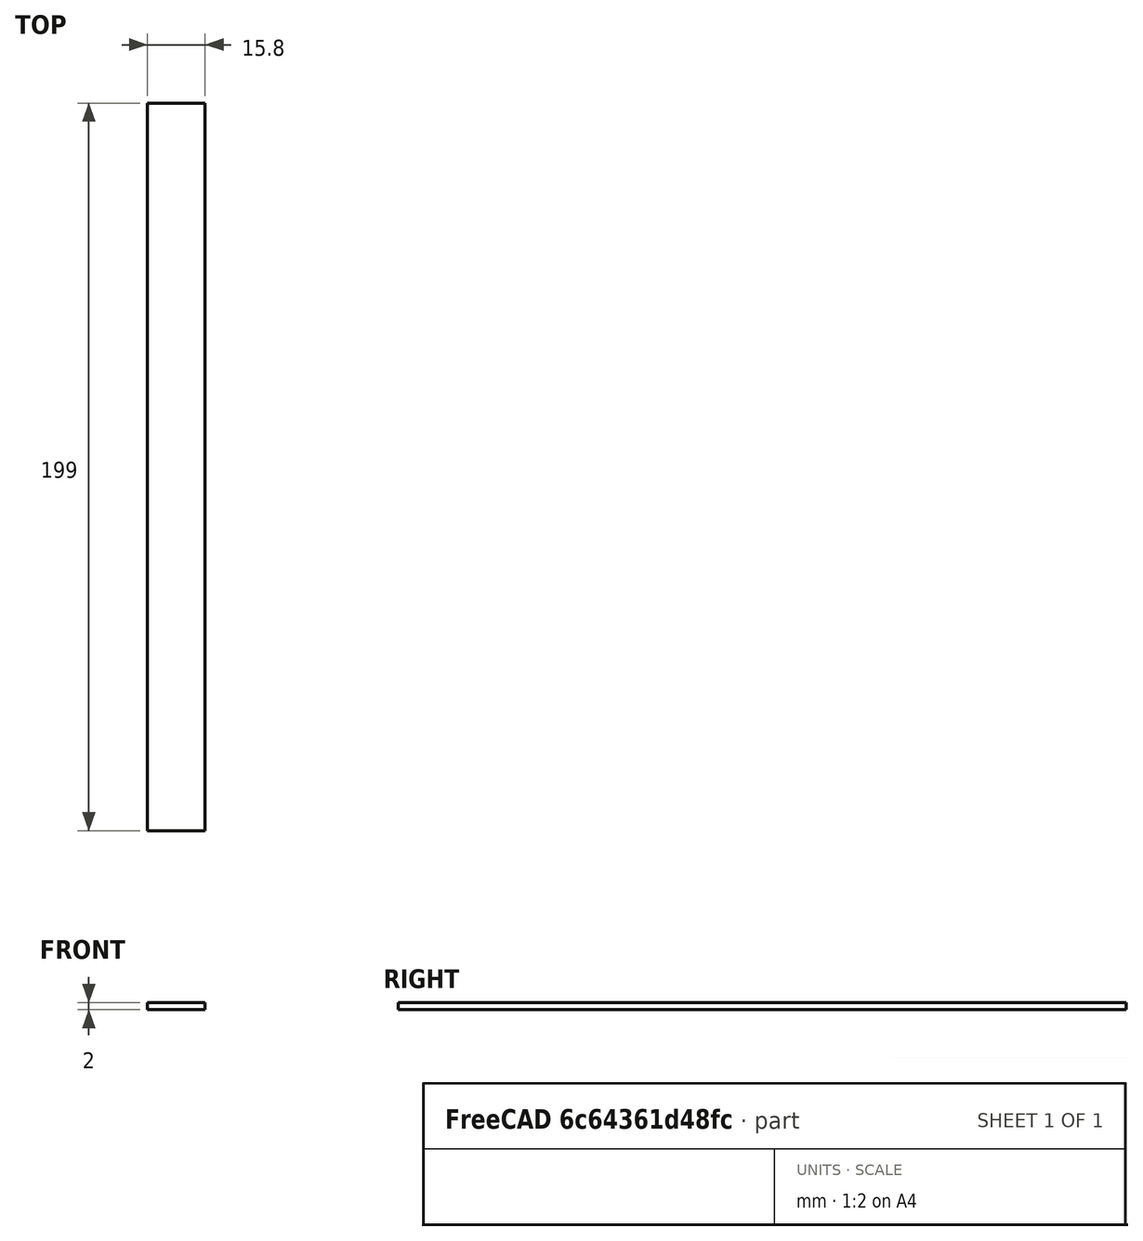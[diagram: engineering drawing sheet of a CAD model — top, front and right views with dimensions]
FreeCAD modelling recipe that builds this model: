
FCSTD DOCUMENT  (FreeCAD 0.19R24276 (Git))
Label: plat_16_199
License: All rights reserved
LicenseURL: http://en.wikipedia.org/wiki/All_rights_reserved
objects: Sketcher::SketchObject×1, PartDesign::Pad×1, PartDesign::Body×1
note: 4 computed .brp shape members not serialized (recipe doc carries the construction recipe); baked Part::Feature solids carry a one-line shape summary decoded from their .brp

FEATURE [Sketcher::SketchObject] Sketch
  FullyConstrained = true
  MapMode = 5
  Support = -> [XY_Plane]
  sketch-geometry (4):
    g0: LineSegment StartX=-7.9 StartY=99.5 StartZ=0 EndX=7.9 EndY=99.5 EndZ=0
    g1: LineSegment StartX=7.9 StartY=99.5 StartZ=0 EndX=7.9 EndY=-99.5 EndZ=0
    g2: LineSegment StartX=7.9 StartY=-99.5 StartZ=0 EndX=-7.9 EndY=-99.5 EndZ=0
    g3: LineSegment StartX=-7.9 StartY=-99.5 StartZ=0 EndX=-7.9 EndY=99.5 EndZ=0
  constraints (10):
    c: Coincident(g0,g1)
    c: Coincident(g1,g2)
    c: Coincident(g2,g3)
    c: Coincident(g3,g0)
    c: Horizontal(g2)
    c: Vertical(g1)
    c: DistanceX(g0,g0) = 15.8
    c: DistanceY(g1,g1) = 199
    c: Symmetric(g0,g0,g-2)
    c: Symmetric(g0,g2,g-1)
FEATURE [PartDesign::Pad] Pad  label="Pad_2mm"
  Direction = (1,1,1)
  Length = 2
  Length2 = 100
  Profile = -> Sketch
  Type = 0
FEATURE [PartDesign::Body] Body
  Group = -> [Sketch,Pad]
  Origin = -> Origin
  Tip = -> Pad
